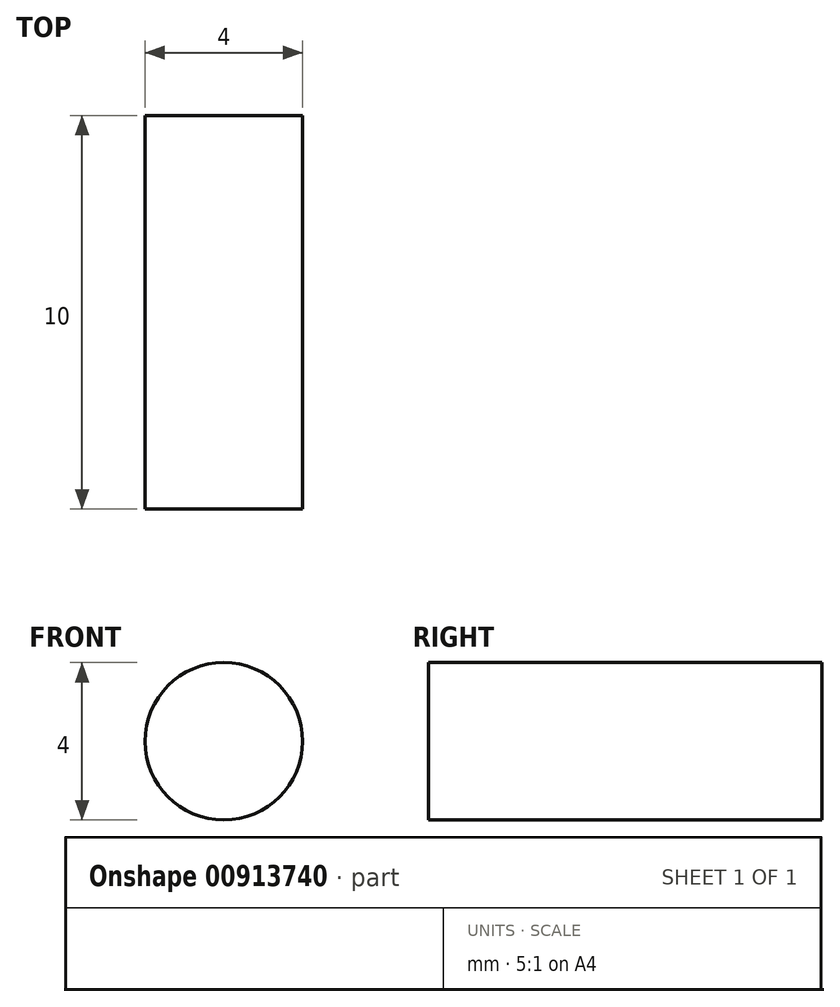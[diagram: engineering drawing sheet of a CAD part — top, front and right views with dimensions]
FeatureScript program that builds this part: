
annotation { "Feature Type Name" : "Feature", "Feature Type Description" : "" }
export const myFeature = defineFeature(function(context is Context, id is Id, definition is map)
    precondition{}
    {
        {
            var Q0;
            Q0=qCreatedBy(makeId("Front.planeOp"),FACE);
            var sketch = newSketch(context, id + "F0", { "sketchPlane" : qUnion([Q0])});
            skCircle(sketch, "E0", {"center": v(0, 0) * mm, "radius": 2 * mm});
            skSolve(sketch);
        }
        {
            var Q0;
            Q0=makeQuery(id+"F0.imprint","IMPRINT",FACE,{"disambiguationData":[TD([[makeQuery(id+"F0.imprint","IMPRINT",EDGE,{"derivedFrom":sQuery(id+"F0.wireOp",EDGE,"E0")}),1.0]])]});
            extrude(context, id + "F1", {"entities" : qUnion([Q0]), "depth" : 5 * mm, "offsetDistance" : 25 * mm, "hasSecondDirection" : true, "secondDirectionOppositeDirection" : true, "secondDirectionDepth" : 5 * mm});
        }
    });
